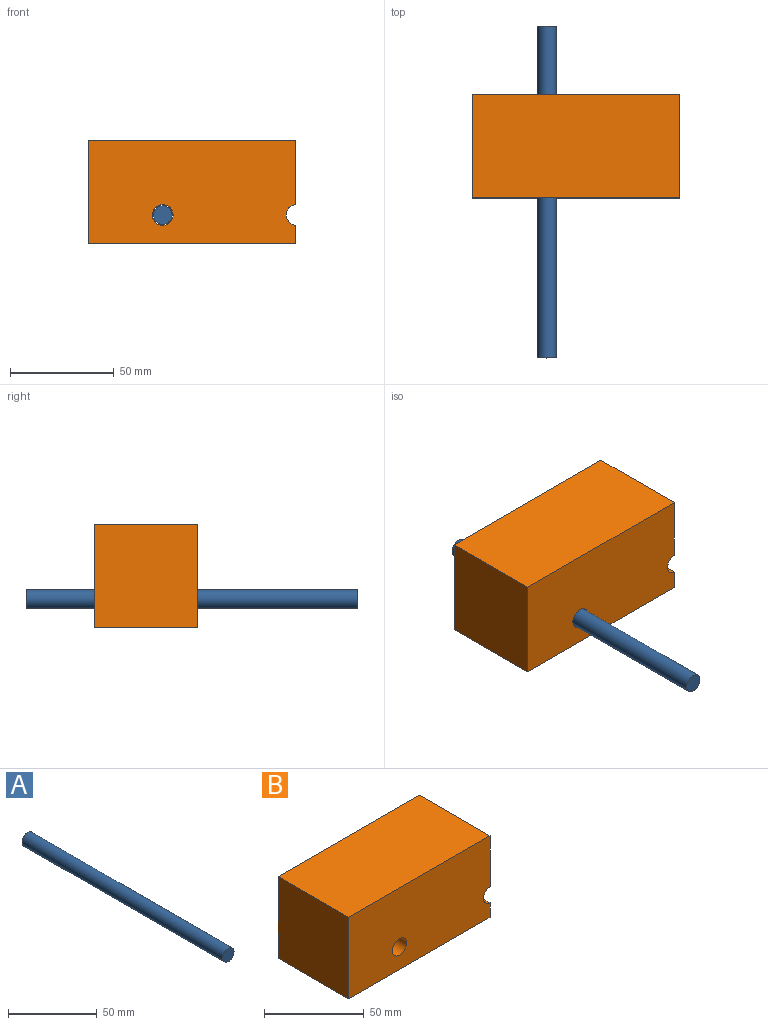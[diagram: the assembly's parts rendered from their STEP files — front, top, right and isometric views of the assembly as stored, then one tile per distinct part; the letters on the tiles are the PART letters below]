
ASSEMBLY  parts=2 mates=1
PART A: 3 faces, bbox 9x160x9 mm
  f0: cylinder r=4.5mm len=160mm, axis (0,1,0), area 4523.9mm2, adj f1,f2
  f1: plane 9x9mm, normal (0,-1,0), area 63.6mm2, adj f0
  f2: plane 9x9mm, normal (0,1,0), area 63.6mm2, adj f0
PART B: 9 faces, bbox 100x50x50 mm
  f0: plane 100x50mm, normal (0,1,0), area 4886.2mm2, adj f2,f3,f4,f5,f6,f7,f8
  f1: plane 100x50mm, normal (0,-1,0), area 4886.2mm2, adj f2,f3,f4,f5,f6,f7,f8
  f2: plane 50x31.08mm, normal (1,0,0), area 1553.8mm2, adj f0,f1,f5,f7
  f3: plane 50x8.96mm, normal (1,0,0), area 447.9mm2, adj f0,f1,f6,f7
  f4: plane 50x50mm, normal (-1,0,0), area 2500mm2, adj f0,f1,f5,f6
  f5: plane 100x50mm, normal (0,0,1), area 5000mm2, adj f0,f1,f2,f4
  f6: plane 100x50mm, normal (0,0,-1), area 5000mm2, adj f0,f1,f3,f4
  f7: cylinder r=5mm len=50mm, axis (0,-1,0), area 744.7mm2, adj f0,f1,f2,f3
  f8: cylinder r=5mm len=50mm, axis (0,-1,0), area 1570.8mm2, adj f0,f1
PLACE A t=(16.44,-11.13,50.78)mm
PLACE B t=(21.31,0,36.84)mm
MATE cylindrical A.f0 <-> B.f8  axis (0,-1,0) through (16.44,-91.13,50.78)mm
